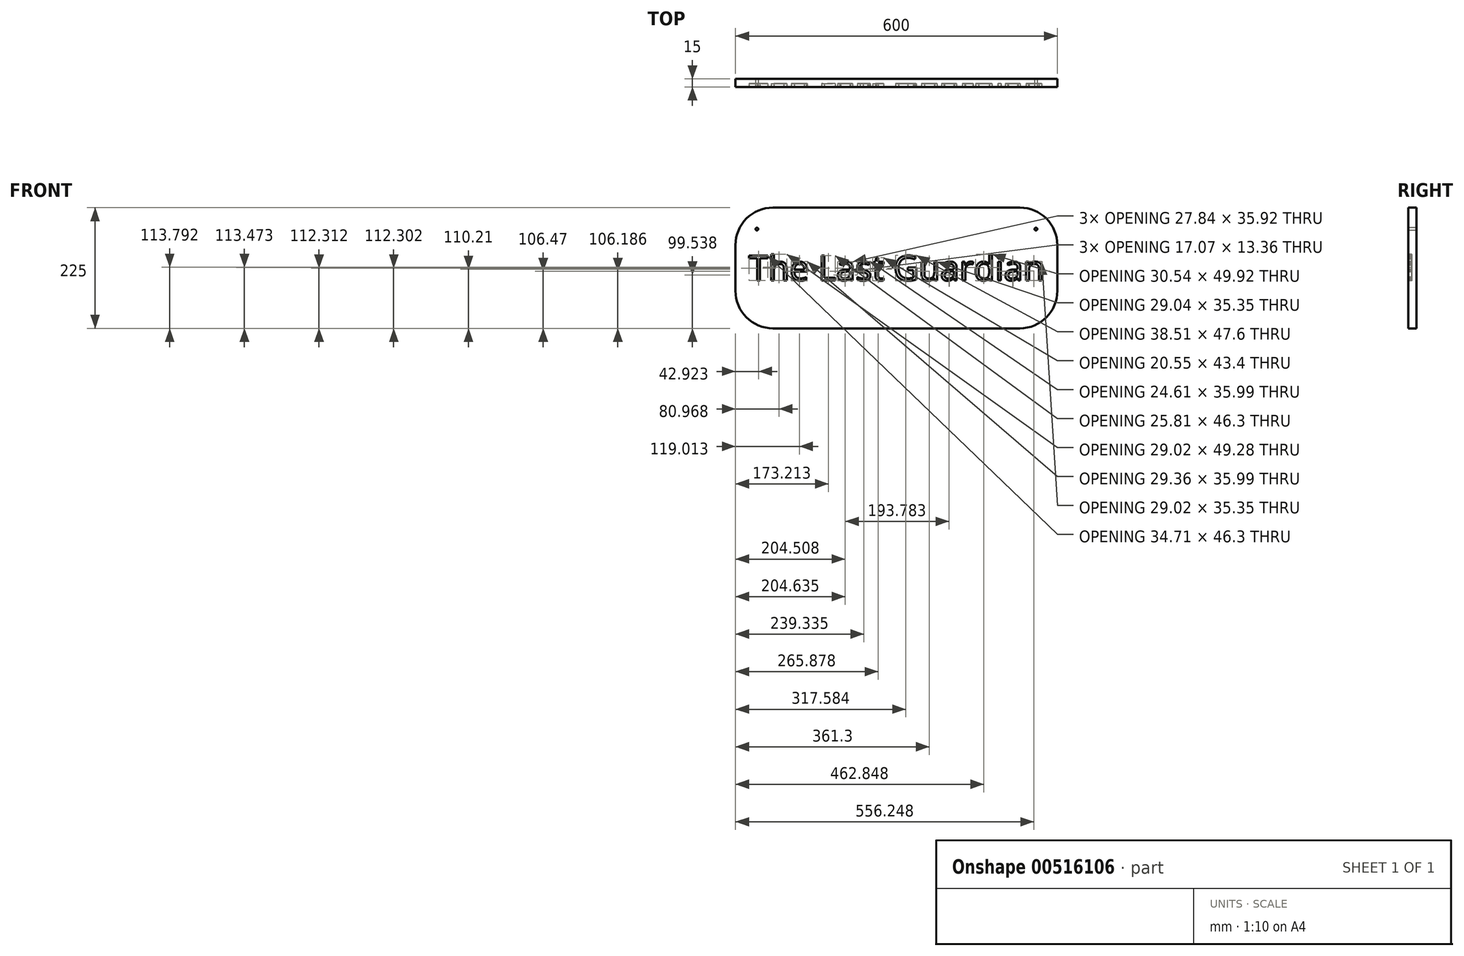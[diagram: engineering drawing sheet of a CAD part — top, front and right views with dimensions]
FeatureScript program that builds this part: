
annotation { "Feature Type Name" : "Feature", "Feature Type Description" : "" }
export const myFeature = defineFeature(function(context is Context, id is Id, definition is map)
    precondition{}
    {
        {
            var Q0;
            Q0=qCreatedBy(makeId("Front.planeOp"),FACE);
            var sketch = newSketch(context, id + "F0", { "sketchPlane" : qUnion([Q0])});
            skLineSegment(sketch, "E0.bottom", {"start": v(300, 112.5) * mm, "end": v(-300, 112.5) * mm});
            skLineSegment(sketch, "E0.top", {"start": v(300, -112.5) * mm, "end": v(-300, -112.5) * mm});
            skLineSegment(sketch, "E0.left", {"start": v(300, 112.5) * mm, "end": v(300, -112.5) * mm});
            skLineSegment(sketch, "E0.right", {"start": v(-300, 112.5) * mm, "end": v(-300, -112.5) * mm});
            skPoint(sketch, "E0.middle", {"position": v(0, 0) * mm});
            skSolve(sketch);
        }
        {
            var Q0;
            Q0=makeQuery(id+"F0.imprint","IMPRINT",FACE,{"disambiguationData":[TD([[makeQuery(id+"F0.imprint","IMPRINT",EDGE,{"derivedFrom":sQuery(id+"F0.wireOp",EDGE,"E0.bottom")}),1.0]])]});
            extrude(context, id + "F1", {"entities" : qUnion([Q0]), "depth" : 15 * mm, "offsetDistance" : 25 * mm});
        }
        {
            var Q0;
            Q0=makeQuery(id+"F1.opExtrude","CAP_FACE",FACE,{"disambiguationData":[OSD([sQuery(id+"F0.wireOp",EDGE,"E0.bottom"),sQuery(id+"F0.wireOp",EDGE,"E0.top"),sQuery(id+"F0.wireOp",EDGE,"E0.left"),sQuery(id+"F0.wireOp",EDGE,"E0.right")])],"isStart":false});
            var sketch = newSketch(context, id + "F2", { "sketchPlane" : qUnion([Q0])});
            skText(sketch, "E1", { "text": "The Last Guardian", "fontName": "OpenSans-Regular.ttf"});
            const initialGuessF2  = {"E1": [-0.275, -0.02335, 1, 0, 0.0467]};
            skSetInitialGuess(sketch, initialGuessF2);
            skSolve(sketch);
        }
        {
            var Q0;
            Q0=makeQuery(id+"F1.opExtrude","SWEPT_EDGE",EDGE,{"disambiguationData":[OSD([sQuery(id+"F0.wireOp",EDGE,"E0.bottom"),sQuery(id+"F0.wireOp",EDGE,"E0.left")])]});
            var Q1;
            Q1=makeQuery(id+"F1.opExtrude","SWEPT_EDGE",EDGE,{"disambiguationData":[OSD([sQuery(id+"F0.wireOp",EDGE,"E0.top"),sQuery(id+"F0.wireOp",EDGE,"E0.left")])]});
            var Q2;
            Q2=makeQuery(id+"F1.opExtrude","SWEPT_EDGE",EDGE,{"disambiguationData":[OSD([sQuery(id+"F0.wireOp",EDGE,"E0.top"),sQuery(id+"F0.wireOp",EDGE,"E0.right")])]});
            var Q3;
            Q3=makeQuery(id+"F1.opExtrude","SWEPT_EDGE",EDGE,{"disambiguationData":[OSD([sQuery(id+"F0.wireOp",EDGE,"E0.bottom"),sQuery(id+"F0.wireOp",EDGE,"E0.right")])]});
            fillet(context, id + "F3", {"entities" : qUnion([Q0, Q1, Q2, Q3]), "radius" : 70 * mm, "tangentPropagation" : true, "allowEdgeOverflow" : false});
        }
        {
            var Q0;
            Q0 = qSketchRegion(id + "F2", true);
            extrude(context, id + "F4", {"entities" : qUnion([Q0]), "operationType" : NewBodyOperationType.REMOVE, "oppositeDirection" : true, "depth" : 6 * mm, "offsetDistance" : 25 * mm});
        }
        {
            var Q0;
            {var subQ0=sQuery(id+"F0.wireOp",EDGE,"E0.right");var subQ1=sQuery(id+"F0.wireOp",EDGE,"E0.top");var subQ2=sQuery(id+"F0.wireOp",EDGE,"E0.left");var subQ3=sQuery(id+"F0.wireOp",EDGE,"E0.bottom");Q0=makeQuery(id+"F4.boolean.opBoolean","SPLIT",FACE,{"disambiguationData":[TD([makeQuery(id+"F1.opExtrude","SWEPT_FACE",FACE,{"disambiguationData":[OSD([subQ3])]})])],"derivedFrom":makeQuery(id+"F1.opExtrude","CAP_FACE",FACE,{"disambiguationData":[OSD([subQ3,subQ1,subQ2,subQ0])],"isStart":false})});}
            var sketch = newSketch(context, id + "F5", { "sketchPlane" : qUnion([Q0])});
            skCircle(sketch, "E2", {"center": v(-260, 72.5) * mm, "radius": 2.5 * mm});
            skCircle(sketch, "E3", {"center": v(260, 72.5) * mm, "radius": 2.5 * mm});
            skSolve(sketch);
        }
        {
            var Q0;
            Q0 = qSketchRegion(id + "F5", true);
            extrude(context, id + "F6", {"entities" : qUnion([Q0]), "operationType" : NewBodyOperationType.REMOVE, "oppositeDirection" : true, "depth" : 25 * mm, "offsetDistance" : 25 * mm});
        }
        {
            var Q0;
            Q0=makeQuery(id+"F1.opExtrude","SWEPT_BODY",BODY,{"disambiguationData":[OSD([sQuery(id+"F0.wireOp",EDGE,"E0.bottom"),sQuery(id+"F0.wireOp",EDGE,"E0.top"),sQuery(id+"F0.wireOp",EDGE,"E0.left"),sQuery(id+"F0.wireOp",EDGE,"E0.right")])]});
            transform(context, id + "F7", {"entities" : qUnion([Q0]), "transformType" : TransformType.TRANSLATION_3D, "dx" : 0 * mm, "dy" : 0 * mm, "dz" : 0 * mm, "makeCopy" : true});
        }
    });
